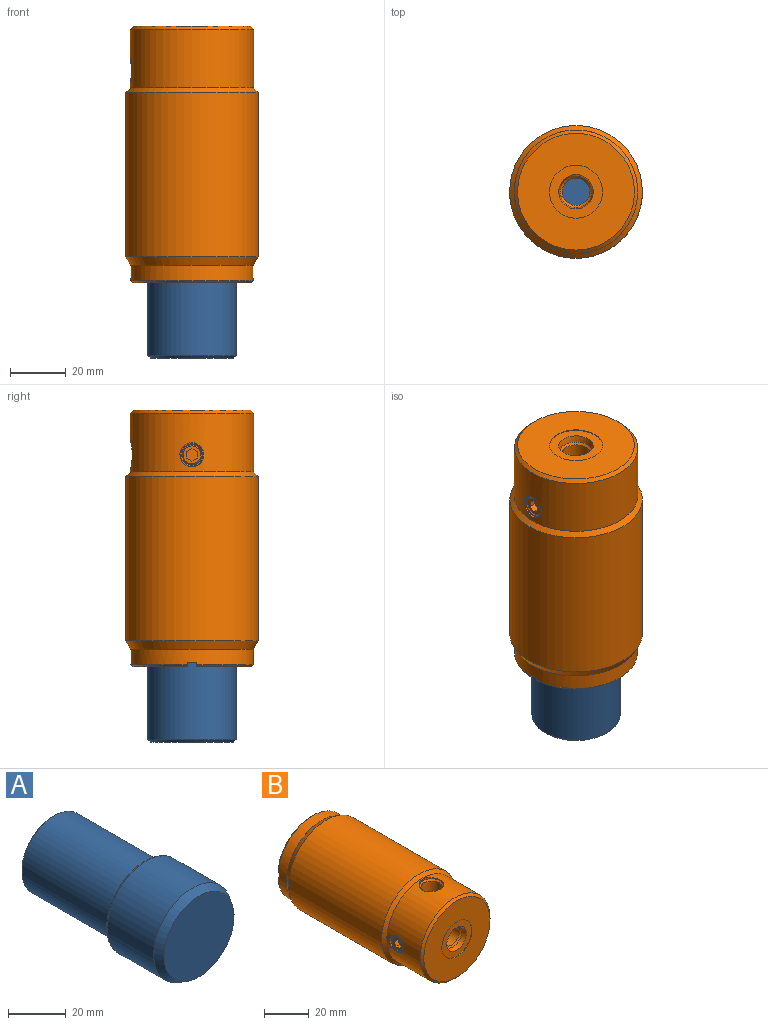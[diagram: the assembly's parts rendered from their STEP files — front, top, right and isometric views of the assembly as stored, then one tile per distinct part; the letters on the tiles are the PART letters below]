
ASSEMBLY  parts=2 mates=1
PART A: 13 faces, bbox 41.1x71.6x41.1 mm
  f0: cone r=3.43mm half-angle=30deg, axis (0,1,0), area 10.5mm2, adj f1,f10
  f1: cylinder r=3.17mm len=6.35mm, axis (0,1,0), area 117.9mm2, adj f0,f12
  f2: cylinder r=2.77mm len=5.54mm, axis (0,1,0), area 28.7mm2, adj f11,f12
  f3: cone r=15.84mm half-angle=45deg, axis (0,-1,0), area 104.7mm2, adj f4,f10
  f4: cylinder r=15.84mm len=44.2mm, axis (0,-1,0), area 4397.8mm2, adj f3,f9
  f5: torus R=18.24mm, axis (0,-1,0), area 140.8mm2, adj f6,f9
  f6: cylinder r=19mm len=38mm, axis (0,-1,0), area 2713.8mm2, adj f5,f7
  f7: cone r=17.17mm half-angle=30deg, axis (0,1,0), area 416.5mm2, adj f6,f8
  f8: plane 34.33x34.33mm, normal (0,-1,0), area 925.8mm2, adj f7
  f9: plane 36.47x36.47mm, normal (0,1,0), area 256.9mm2, adj f4,f5
  f10: plane 30.15x30.15mm, normal (0,1,0), area 677mm2, adj f0,f3
  f11: plane 5.54x5.54mm, normal (0,1,0), area 24.1mm2, adj f2
  f12: plane 6.35x6.35mm, normal (0,1,0), area 7.6mm2, adj f1,f2
PART B: 46 faces, bbox 47.6x92.2x47.6 mm
  f0: cylinder r=4.32mm len=8.64mm, axis (1,0,0), area 14.9mm2, adj f20,f38
  f1: cone r=3.59mm half-angle=45deg, axis (-1,0,0), area 12.8mm2, adj f2,f38
  f2: cone r=3.21mm half-angle=45deg, axis (1,0,0), area 11.5mm2, adj f1,f37
  f3: cone r=5.46mm half-angle=45deg, axis (0,0,1), area 32.5mm2, adj f4,f35
  f4: cone r=4.74mm half-angle=1.7deg, axis (0,0,1), area 181.5mm2, adj f3,f36
  f5: cylinder r=4.22mm len=11.62mm, axis (0,0,1), area 274.3mm2, adj f10,f36
  f6: cylinder r=5.55mm len=11.1mm, axis (0,0,1), area 23.2mm2, adj f20,f35
  f7: cylinder r=9.53mm len=19.05mm, axis (0,-1,0), area 15.2mm2, adj f27,f28
  f8: cone r=5.68mm half-angle=12deg, axis (0,-1,0), area 90mm2, adj f9,f27
  f9: cone r=4.95mm half-angle=45deg, axis (0,-1,0), area 34.5mm2, adj f8,f10
  f10: cylinder r=4.95mm len=18.8mm, axis (0,-1,0), area 521.9mm2, adj f5,f9,f26
  f11: cone r=19.06mm half-angle=45deg, axis (0,1,0), area 257.7mm2, adj f12,f26
  f12: cylinder r=19.06mm len=50.56mm, axis (0,-1,0), area 6055.6mm2, adj f11,f25
  f13: cylinder r=15.89mm len=31.78mm, axis (0,-1,0), area 1777.5mm2, adj f22,f24,f25,f29,f30,f31,f32,f33
  f14: cone r=22.03mm half-angle=45deg, axis (0,-1,0), area 69.7mm2, adj f15,f24,f30,f32
  f15: cylinder r=22.03mm len=44.07mm, axis (0,-1,0), area 768.6mm2, adj f14,f21,f23,f29,f30,f31,f32,f33
  f16: cone r=23.81mm half-angle=30deg, axis (0,-1,0), area 494.6mm2, adj f17,f23
  f17: cylinder r=23.81mm len=59.01mm, axis (0,-1,0), area 8828.4mm2, adj f16,f18
  f18: cone r=22.16mm half-angle=45deg, axis (0,1,0), area 337.2mm2, adj f17,f20
  f19: cone r=20.97mm half-angle=45deg, axis (0,1,0), area 228.2mm2, adj f20,f28
  f20: cylinder r=22.16mm len=44.32mm, axis (0,-1,0), area 2772.9mm2, adj f0,f6,f18,f19
  f21: cone r=22.03mm half-angle=45deg, axis (0,-1,0), area 69.7mm2, adj f15,f22,f31,f34
  f22: plane 42.42x19.62mm, normal (0,1,0), area 296.5mm2, adj f13,f21,f31,f34
  f23: plane 44.2x44.2mm, normal (0,1,0), area 8.8mm2, adj f15,f16
  f24: plane 42.42x19.62mm, normal (0,1,0), area 296.5mm2, adj f13,f14,f30,f32
  f25: plane 38.13x38.13mm, normal (0,-1,0), area 348.6mm2, adj f12,f13
  f26: plane 34.95x34.95mm, normal (0,1,0), area 882.3mm2, adj f10,f11
  f27: plane 19.05x19.05mm, normal (0,-1,0), area 164.8mm2, adj f7,f8
  f28: plane 41.94x41.94mm, normal (0,-1,0), area 1096.6mm2, adj f7,f19
  f29: plane 6.23x3.3mm, normal (0,1,0), area 20.3mm2, adj f13,f15,f30,f31
  f30: plane 6.17x1.53mm, normal (0,0,1), area 9.1mm2, adj f13,f14,f15,f24,f29
  f31: plane 6.17x1.53mm, normal (0,0,-1), area 9.1mm2, adj f13,f15,f21,f22,f29
  f32: plane 6.17x1.53mm, normal (0,0,1), area 9.1mm2, adj f13,f14,f15,f24,f33
  f33: plane 6.23x3.3mm, normal (0,1,0), area 20.3mm2, adj f13,f15,f32,f34
  f34: plane 6.17x1.53mm, normal (0,0,-1), area 9.1mm2, adj f13,f15,f21,f22,f33
  f35: plane 11.1x11.1mm, normal (0,0,1), area 3.1mm2, adj f3,f6
  f36: plane 9.12x9.12mm, normal (0,0,1), area 9.4mm2, adj f4,f5
  f37: plane 6.41x6.41mm, normal (-1,0,0), area 18.7mm2, adj f2,f39,f40,f41,f42,f43,f44
  f38: plane 8.64x8.64mm, normal (-1,0,0), area 9.1mm2, adj f0,f1
  f39: plane 2.29x1.98mm, normal (0,0.87,0.5), area 5.2mm2, adj f37,f40,f44,f45
  f40: plane 2.29x2.29mm, normal (0,0,1), area 5.2mm2, adj f37,f39,f41,f45
  f41: plane 2.29x1.98mm, normal (0,-0.87,0.5), area 5.2mm2, adj f37,f40,f42,f45
  f42: plane 2.29x1.98mm, normal (0,-0.87,-0.5), area 5.2mm2, adj f37,f41,f43,f45
  f43: plane 2.29x2.29mm, normal (0,0,-1), area 5.2mm2, adj f37,f42,f44,f45
  f44: plane 2.29x1.98mm, normal (0,0.87,-0.5), area 5.2mm2, adj f37,f39,f43,f45
  f45: plane 4.58x3.96mm, normal (-1,0,0), area 13.6mm2, adj f39,f40,f41,f42,f43,f44
PLACE A rot(axis=(-1,0,0),90deg) t=(0,0,-25.48)mm
PLACE B rot(axis=(-1,0,0),90deg) t=(0,0,0)mm
MATE slider A.f0 <-> B.f7  axis (0,0,1) through (0,0,-74.3)mm
